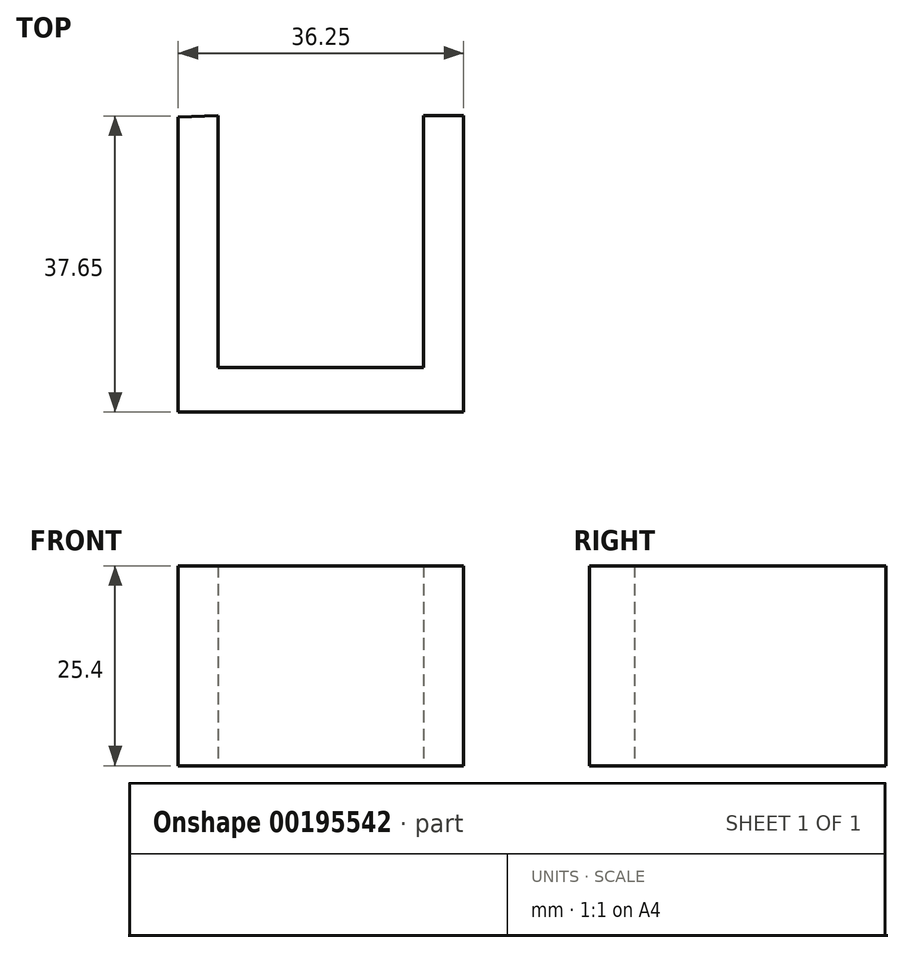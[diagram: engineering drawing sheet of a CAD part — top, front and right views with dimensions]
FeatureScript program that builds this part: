
annotation { "Feature Type Name" : "Feature", "Feature Type Description" : "" }
export const myFeature = defineFeature(function(context is Context, id is Id, definition is map)
    precondition{}
    {
        {
            var Q0;
            Q0=qCreatedBy(makeId("Top.planeOp"),FACE);
            var sketch = newSketch(context, id + "F0", { "sketchPlane" : qUnion([Q0])});
            skLineSegment(sketch, "E0", {"start": v(-36.25, 40.13) * mm, "end": v(-36.25, 2.64) * mm});
            skLineSegment(sketch, "E1", {"start": v(-36.25, 2.64) * mm, "end": v(0, 2.64) * mm});
            skLineSegment(sketch, "E2", {"start": v(0, 2.64) * mm, "end": v(0, 40.3) * mm});
            skLineSegment(sketch, "E3", {"start": v(0, 40.3) * mm, "end": v(-5.08, 40.3) * mm});
            skLineSegment(sketch, "E4", {"start": v(-5.08, 40.3) * mm, "end": v(-5.08, 8.32) * mm});
            skLineSegment(sketch, "E5", {"start": v(-5.08, 8.32) * mm, "end": v(-31.18, 8.32) * mm});
            skLineSegment(sketch, "E6", {"start": v(-31.18, 8.32) * mm, "end": v(-31.18, 40.3) * mm});
            skLineSegment(sketch, "E7", {"start": v(-31.18, 40.3) * mm, "end": v(-36.25, 40.13) * mm});
            skSolve(sketch);
        }
        {
            var Q0;
            Q0 = qSketchRegion(id + "F0", true);
            extrude(context, id + "F1", {"entities" : qUnion([Q0]), "depth" : 25.4 * mm});
        }
    });
